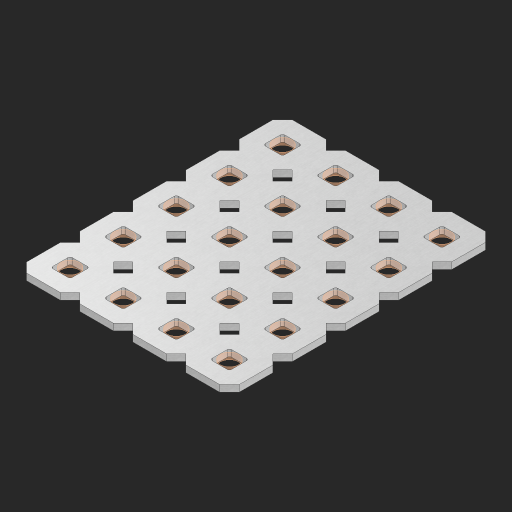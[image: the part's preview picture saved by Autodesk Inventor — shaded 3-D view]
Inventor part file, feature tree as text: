
AUTODESK INVENTOR PART (.ipt)
format: ipt  version: 2023 (Build 270158000, 158)  size: 529,408 bytes
history: native  units: in
note: dims shown in document units (in); Inventor stores cm internally (conversion verified against a paired STEP export)
features: other x21, extrude x19, sketch x2, pattern_linear x1
ambient origin geometry x8: Origin, YZ Plane, XZ Plane, XY Plane, X Axis, Y Axis, Z Axis, Center Point
bodies: Solid1 (feature_tree), Body (feature_tree)
feature tree (43):
  pattern_linear  "Rectangular Pattern1"  Spacing1=0.09in  [1 undecoded]
  sketch  "Sketch1"  dims[d1=0.5in]
  sketch  "Sketch2"  dims[d2=0.182in d3=0.09in d4=0.09in d5=0.09in d6=0.09in d7=0.09in d8=0.09in d9=0.09in d10=0.09in d11=0.02in d13=0.0in d14=0.172in d15=0.0625in d16=0.0in d19=0.5in d22=0.5in]
  other  "Srf1"
  other  "Srf126"
  other  "Srf127"
  other  "Srf128"
  other  "Srf129"
  other  "Srf268"
  other  "Srf269"
  other  "Srf270"
  other  "Srf271"
  other  "Srf272"
  other  "Srf293"
  other  "Srf294"
  other  "Srf295"
  other  "Srf296"
  other  "Srf297"
  other  "Srf318"
  other  "Srf319"
  other  "Srf320"
  other  "Srf321"
  other  "Srf322"
  other  "Circle"
  extrude  "ExtrusionSrf126"  Depth=0.09in
  extrude  "ExtrusionSrf127"  Depth=0.09in
  extrude  "ExtrusionSrf128"  Depth=0.09in
  extrude  "ExtrusionSrf129"  Depth=0.09in
  extrude  "ExtrusionSrf268"  Depth=0.09in
  extrude  "ExtrusionSrf269"  Depth=0.09in
  extrude  "ExtrusionSrf270"  Depth=0.09in
  extrude  "ExtrusionSrf271"  Depth=0.02in
  extrude  "ExtrusionSrf272"  TaperAngle=0.0deg  [1 undecoded]
  extrude  "ExtrusionSrf293"  Depth=0.5in
  extrude  "ExtrusionSrf294"  Depth=0.0625in TaperAngle=0.0deg
  extrude  "ExtrusionSrf295"  Depth=0.5in
  extrude  "ExtrusionSrf296"  Depth=0.5in
  extrude  "ExtrusionSrf297"  [1 undecoded]
  extrude  "ExtrusionSrf318"  [1 undecoded]
  extrude  "ExtrusionSrf319"  [1 undecoded]
  extrude  "ExtrusionSrf320"  [1 undecoded]
  extrude  "ExtrusionSrf321"  [1 undecoded]
  extrude  "ExtrusionSrf322"  [1 undecoded]
note: 8 required parameter values undecoded (feature->parameter linkage not recoverable at this tier; creation-order binding heuristic only, values carry confidence <= 0.55)
